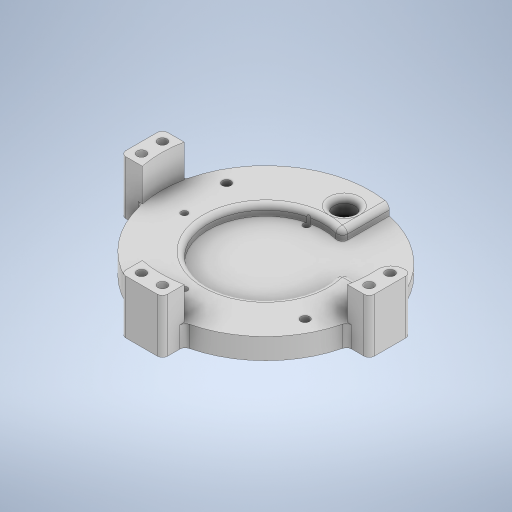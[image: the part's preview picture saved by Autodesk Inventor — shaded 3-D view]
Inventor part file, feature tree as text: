
AUTODESK INVENTOR PART (.ipt)
format: ipt  version: 2023 (Build 270158000, 158)  size: 498,176 bytes
history: native  units: in
note: dims shown in document units (in); Inventor stores cm internally (conversion verified against a paired STEP export)
features: sketch x15, extrude x11, fillet x8, hole x3
ambient origin geometry x8: Origin, YZ Plane, XZ Plane, XY Plane, X Axis, Y Axis, Z Axis, Center Point
bodies: Solid1 (feature_tree)
feature tree (37):
  extrude  "Extrusion1"  Depth=0.2in TaperAngle=0.0deg
  extrude  "Extrusion2"  Depth=0.2in TaperAngle=0.0deg
  extrude  "Extrusion3"  Depth=0.5in
  extrude  "Extrusion4"  Depth=0.4in
  fillet  "Fillet1"  Radius=0.5in
  fillet  "Fillet2"  Radius=0.5in
  fillet  "Fillet3"  Radius=0.4in
  extrude  "Extrusion5"  Depth=0.4in TaperAngle=0.0deg
  extrude  "Extrusion6"  Depth=0.2in
  extrude  "Extrusion8"  Depth=0.2in
  fillet  "Fillet4"  Radius=0.4in
  extrude  "Extrusion9"  Depth=0.2in
  sketch  "Sketch10"  dims[d26=0.4in d30=0.177in]
  hole  "Hole1"  [1 undecoded]
  extrude  "Extrusion10"  Depth=0.177in
  hole  "Hole2"  [1 undecoded]
  fillet  "Fillet5"  Radius=0.1in
  hole  "Hole3"  [1 undecoded]
  extrude  "Extrusion11"  Depth=0.3in TaperAngle=0.0deg
  fillet  "Fillet7"  Radius=0.3in
  extrude  "Extrusion13"  Depth=0.3in
  fillet  "Fillet8"  Radius=0.3in
  fillet  "Fillet9"  Radius=0.3in
  sketch  "Sketch1"  dims[d0=4.0in d1=0.2in d2=0.0in]
  sketch  "Sketch2"  dims[d3=2.2in d4=0.2in d5=0.0in]
  sketch  "Sketch3"  dims[d6=3.75in d10=0.5in]
  sketch  "Sketch4"  dims[d11=0.4in d12=0.4in d13=0.5in d14=0.5in d15=0.4in]
  sketch  "Sketch5"  dims[d16=0.4in d17=1.025in d18=0.0in]
  sketch  "Sketch6"  dims[d19=0.2in d20=0.2in]
  sketch  "Sketch8"  dims[d21=0.4in d22=0.2in d23=0.4in]
  sketch  "Sketch9"  dims[d24=0.2in d25=0.2in]
  sketch  "Sketch11"  dims[d33=0.177in d34=0.177in]
  sketch  "Sketch12"  dims[d35=0.177in d36=5.0in d37=0.0in d38=0.1in]
  sketch  "Sketch13"  dims[d39=0.1in d40=0.1in]
  sketch  "Sketch14"  dims[d41=0.2in d42=0.0in d43=0.625in d44=0.0in d47=0.3in]
  sketch  "Sketch15"  dims[d48=0.3in d49=0.3in d50=0.3in d51=0.3in]
  sketch  "Sketch17"  dims[d52=0.2in d53=0.0in d54=0.1in d55=0.9in d56=0.8875in d57=0.8875in d58=0.25in d59=0.25in d60=0.2in d61=0.0in d62=0.126in d63=0.432in d64=0.256in d65=0.118in d66=90.0deg d67=0.5in d68=0.8108in d69=1.65in d70=45.0deg d71=1.65in d72=45.0deg d73=0.25in d74=0.2in d75=0.0in d76=0.126in d77=0.75in d78=0.375in d79=0.25in d80=0.5635in d81=1.0in d82=0.8108in d83=0.25in d84=0.4154in d85=0.2in d86=1.5in d87=0.75in d88=1.5in d89=0.75in d90=0.169in d91=0.75in d92=0.315in d93=0.157in d94=0.5635in d95=1.0in d96=0.8108in d97=0.6875in d98=0.0in d102=0.1in d103=1.5in d104=0.4in d105=1.0in d106=0.0in d107=0.1in d108=0.1in]
note: 3 required parameter values undecoded (feature->parameter linkage not recoverable at this tier; creation-order binding heuristic only, values carry confidence <= 0.55)
